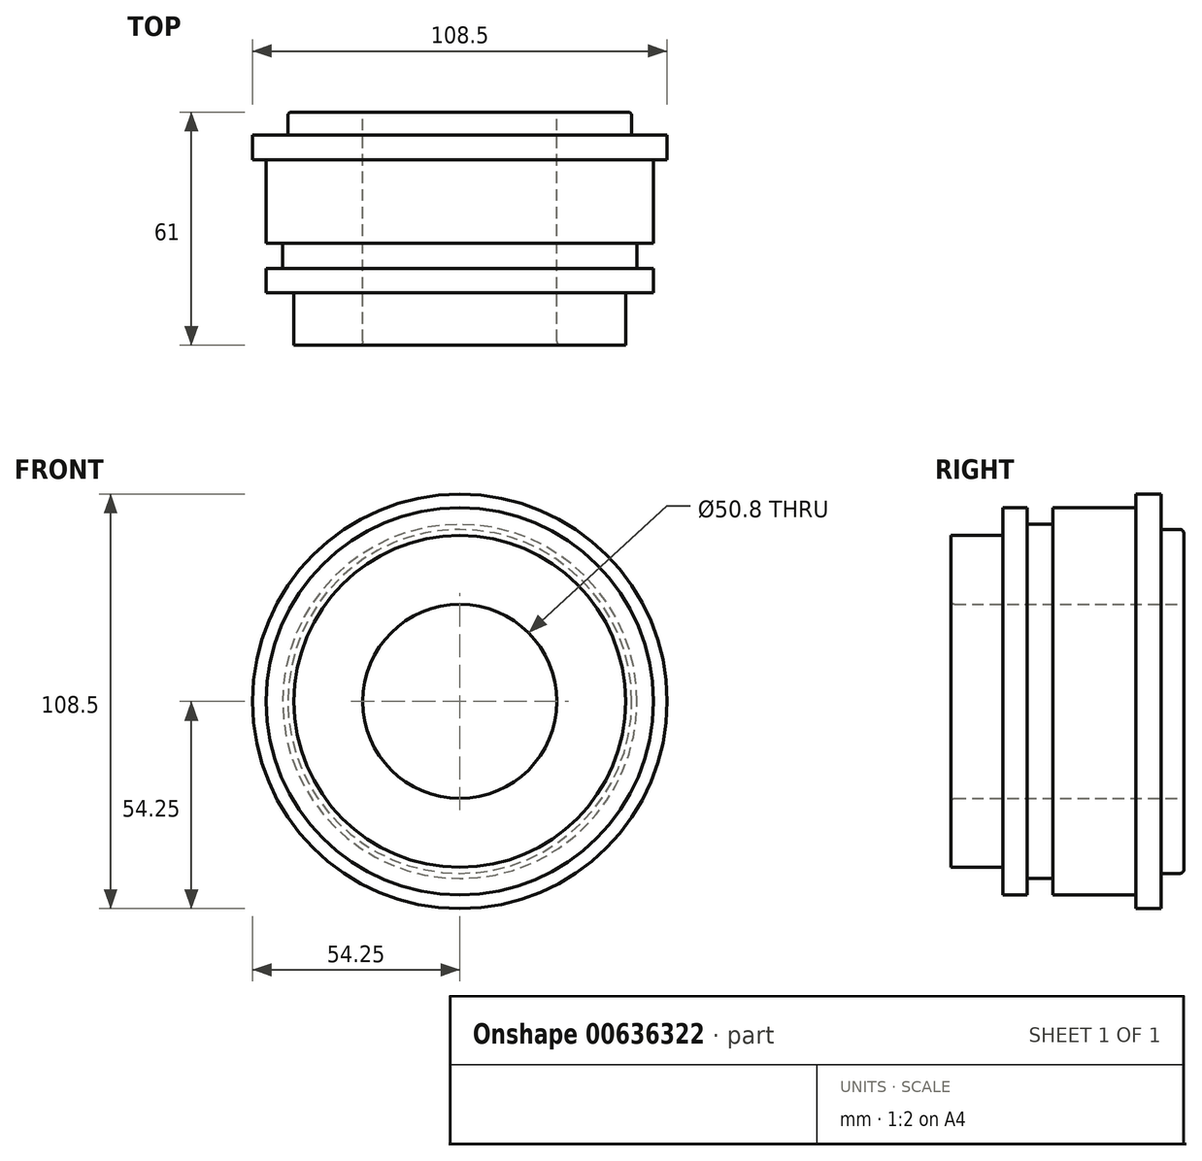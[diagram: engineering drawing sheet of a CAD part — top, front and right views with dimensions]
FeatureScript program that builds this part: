
annotation { "Feature Type Name" : "Feature", "Feature Type Description" : "" }
export const myFeature = defineFeature(function(context is Context, id is Id, definition is map)
    precondition{}
    {
        {
            var Q0;
            Q0=qCreatedBy(makeId("Front.planeOp"),FACE);
            var sketch = newSketch(context, id + "F0", { "sketchPlane" : qUnion([Q0])});
            skCircle(sketch, "E0", {"center": v(0, 0) * mm, "radius": 54.25 * mm});
            skCircle(sketch, "E1", {"center": v(0, 0) * mm, "radius": 25.4 * mm});
            skSolve(sketch);
        }
        {
            var Q0;
            Q0=makeQuery(id+"F0.imprint","IMPRINT",FACE,{"disambiguationData":[TD([[makeQuery(id+"F0.imprint","IMPRINT",EDGE,{"derivedFrom":sQuery(id+"F0.wireOp",EDGE,"E0")}),1.0]])]});
            extrude(context, id + "F1", {"entities" : qUnion([Q0]), "depth" : 55 * mm, "offsetDistance" : 25 * mm});
        }
        {
            var Q0;
            Q0=makeQuery(id+"F1.opExtrude","CAP_FACE",FACE,{"disambiguationData":[OSD([sQuery(id+"F0.wireOp",EDGE,"E0"),sQuery(id+"F0.wireOp",EDGE,"E1")])],"isStart":false});
            var sketch = newSketch(context, id + "F2", { "sketchPlane" : qUnion([Q0])});
            skCircle(sketch, "E2", {"center": v(0, 0) * mm, "radius": 46.35 * mm});
            skCircle(sketch, "E3", {"center": v(0, 0) * mm, "radius": 55.74 * mm});
            skSolve(sketch);
        }
        {
            var Q0;
            Q0=makeQuery(id+"F2.imprint","IMPRINT",FACE,{"disambiguationData":[TD([[makeQuery(id+"F2.imprint","IMPRINT",EDGE,{"derivedFrom":sQuery(id+"F2.wireOp",EDGE,"E2")}),-1.0]])]});
            extrude(context, id + "F3", {"entities" : qUnion([Q0]), "operationType" : NewBodyOperationType.REMOVE, "oppositeDirection" : true, "depth" : 26.7 * mm, "offsetDistance" : 25 * mm, "hasSecondDirection" : true, "secondDirectionOppositeDirection" : true, "secondDirectionDepth" : 20 * mm});
        }
        {
            var Q0;
            Q0=makeQuery(id+"F1.opExtrude","CAP_FACE",FACE,{"disambiguationData":[OSD([sQuery(id+"F0.wireOp",EDGE,"E0"),sQuery(id+"F0.wireOp",EDGE,"E1")])],"isStart":false});
            var sketch = newSketch(context, id + "F4", { "sketchPlane" : qUnion([Q0])});
            skCircle(sketch, "E4", {"center": v(0, 0) * mm, "radius": 50.7 * mm});
            skSolve(sketch);
        }
        {
            var Q0;
            Q0=makeQuery(id+"F4.imprint","IMPRINT",FACE,{"disambiguationData":[TD([[makeQuery(id+"F4.imprint","IMPRINT",EDGE,{"derivedFrom":sQuery(id+"F4.wireOp",EDGE,"E4")}),-1.0]])]});
            extrude(context, id + "F5", {"entities" : qUnion([Q0]), "operationType" : NewBodyOperationType.REMOVE, "oppositeDirection" : true, "depth" : 48.5 * mm, "offsetDistance" : 25 * mm});
        }
        {
            var Q0;
            Q0=makeQuery(id+"F1.opExtrude","CAP_FACE",FACE,{"disambiguationData":[OSD([sQuery(id+"F0.wireOp",EDGE,"E0"),sQuery(id+"F0.wireOp",EDGE,"E1")])],"isStart":false});
            var sketch = newSketch(context, id + "F6", { "sketchPlane" : qUnion([Q0])});
            skCircle(sketch, "E5", {"center": v(0, 0) * mm, "radius": 43.4 * mm});
            skSolve(sketch);
        }
        {
            var Q0;
            Q0=makeQuery(id+"F6.imprint","IMPRINT",FACE,{"disambiguationData":[TD([[makeQuery(id+"F6.imprint","IMPRINT",EDGE,{"derivedFrom":sQuery(id+"F6.wireOp",EDGE,"E5")}),-1.0]])]});
            extrude(context, id + "F7", {"entities" : qUnion([Q0]), "operationType" : NewBodyOperationType.REMOVE, "oppositeDirection" : true, "depth" : 13.7 * mm, "offsetDistance" : 25 * mm});
        }
        {
            var Q0;
            Q0=makeQuery(id+"F1.opExtrude","CAP_EDGE",EDGE,{"disambiguationData":[OSD([sQuery(id+"F0.wireOp",EDGE,"E1")])],"isStart":false});
            fillet(context, id + "F8", {"entities" : qUnion([Q0]), "radius" : 1 * mm, "tangentPropagation" : true, "allowEdgeOverflow" : false});
        }
        {
            var Q0;
            Q0=qCreatedBy(makeId("Front.planeOp"),FACE);
            var sketch = newSketch(context, id + "F9", { "sketchPlane" : qUnion([Q0])});
            skCircle(sketch, "E6", {"center": v(0, 0) * mm, "radius": 45 * mm});
            skCircle(sketch, "E7", {"center": v(0, 0) * mm, "radius": 25.4 * mm});
            skSolve(sketch);
        }
        {
            var Q0;
            Q0=makeQuery(id+"F9.imprint","IMPRINT",FACE,{"disambiguationData":[TD([[makeQuery(id+"F9.imprint","IMPRINT",EDGE,{"derivedFrom":sQuery(id+"F9.wireOp",EDGE,"E6")}),1.0]])]});
            extrude(context, id + "F10", {"entities" : qUnion([Q0]), "operationType" : NewBodyOperationType.ADD, "oppositeDirection" : true, "depth" : 6 * mm, "offsetDistance" : 25 * mm});
        }
        {
            var Q0;
            Q0=makeQuery(id+"F10.opExtrude","CAP_EDGE",EDGE,{"disambiguationData":[OSD([sQuery(id+"F9.wireOp",EDGE,"E6")])],"isStart":false});
            fillet(context, id + "F11", {"entities" : qUnion([Q0]), "radius" : 1 * mm, "tangentPropagation" : true, "allowEdgeOverflow" : false});
        }
    });
